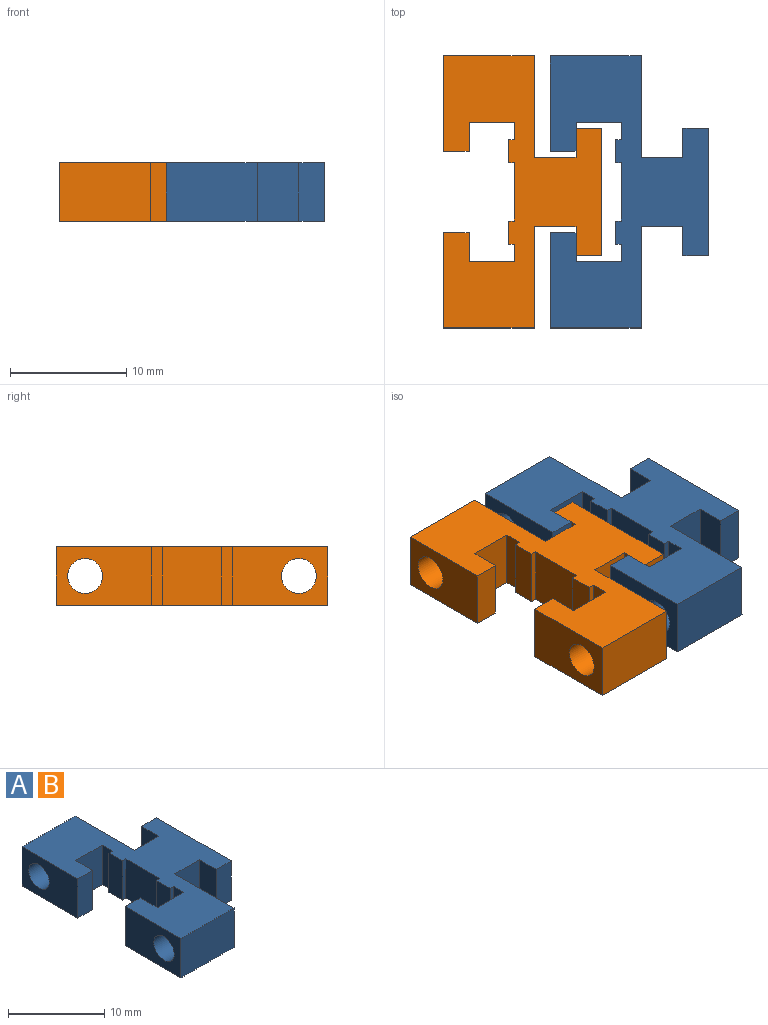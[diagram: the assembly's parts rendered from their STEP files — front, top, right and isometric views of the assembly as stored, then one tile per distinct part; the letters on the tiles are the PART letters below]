
ASSEMBLY  parts=2 mates=1
PART A: 32 faces, bbox 13.6x23.4x5 mm
  f0: plane 8.7x5mm, normal (1,0,0), area 36.4mm2, adj f5,f14,f15,f16,f17
  f1: plane 8.2x5mm, normal (-1,0,0), area 33.9mm2, adj f6,f14,f15,f16,f17
  f2: plane 11x5mm, normal (1,0,0), area 55mm2, adj f3,f14,f15,f20
  f3: plane 5x2.2mm, normal (0,1,0), area 11mm2, adj f2,f4,f14,f15
  f4: plane 5x2.5mm, normal (-1,0,0), area 12.5mm2, adj f3,f5,f14,f15
  f5: plane 5x3.6mm, normal (0,1,0), area 18mm2, adj f0,f4,f14,f15
  f6: plane 5x2.2mm, normal (0,-1,0), area 11mm2, adj f1,f7,f14,f15
  f7: plane 5x2.5mm, normal (1,0,0), area 12.5mm2, adj f6,f8,f14,f15
  f8: plane 5x3.9mm, normal (0,-1,0), area 19.5mm2, adj f7,f9,f14,f15
  f9: plane 5x1.5mm, normal (-1,0,0), area 7.5mm2, adj f8,f10,f14,f15
  f10: plane 5x0.5mm, normal (0,1,0), area 2.5mm2, adj f9,f11,f14,f15
  f11: plane 5x2mm, normal (-1,0,0), area 10mm2, adj f10,f12,f14,f15
  f12: plane 5x0.5mm, normal (0,-1,0), area 2.5mm2, adj f11,f13,f14,f15
  f13: plane 5x5mm, normal (-1,0,0), area 25mm2, adj f12,f14,f15,f29
  f14: plane 23.4x13.6mm, normal (0,0,1), area 168.1mm2, adj f0,f1,f2,f3,f4,f5,f6,f7
  f15: plane 23.4x13.6mm, normal (0,0,-1), area 168.1mm2, adj f0,f1,f2,f3,f4,f5,f6,f7
  f16: cylinder r=1.5mm len=7.8mm, axis (-1,0,0), area 73.5mm2, adj f0,f1
  f17: plane 7.8x5mm, normal (0,1,0), area 39mm2, adj f0,f1,f14,f15
  f18: plane 8.7x5mm, normal (1,0,0), area 36.4mm2, adj f14,f15,f22,f30,f31
  f19: plane 8.2x5mm, normal (-1,0,0), area 33.9mm2, adj f14,f15,f23,f30,f31
  f20: plane 5x2.2mm, normal (0,-1,0), area 11mm2, adj f2,f14,f15,f21
  f21: plane 5x2.5mm, normal (-1,0,0), area 12.5mm2, adj f14,f15,f20,f22
  f22: plane 5x3.6mm, normal (0,-1,0), area 18mm2, adj f14,f15,f18,f21
  f23: plane 5x2.2mm, normal (0,1,0), area 11mm2, adj f14,f15,f19,f24
  f24: plane 5x2.5mm, normal (1,0,0), area 12.5mm2, adj f14,f15,f23,f25
  f25: plane 5x3.9mm, normal (0,1,0), area 19.5mm2, adj f14,f15,f24,f26
  f26: plane 5x1.5mm, normal (-1,0,0), area 7.5mm2, adj f14,f15,f25,f27
  f27: plane 5x0.5mm, normal (0,-1,0), area 2.5mm2, adj f14,f15,f26,f28
  f28: plane 5x2mm, normal (-1,0,0), area 10mm2, adj f14,f15,f27,f29
  f29: plane 5x0.5mm, normal (0,1,0), area 2.5mm2, adj f13,f14,f15,f28
  f30: cylinder r=1.5mm len=7.8mm, axis (-1,0,0), area 73.5mm2, adj f18,f19
  f31: plane 7.8x5mm, normal (0,-1,0), area 39mm2, adj f14,f15,f18,f19
PART B: same geometry as A
PLACE A t=(4.97,1.78,-0.1)mm
PLACE B t=(-4.23,1.78,-0.1)mm fixed
MATE planar A.f6 <-> B.f6  axis (0,-1,0) through (1.07,5.28,2.4)mm
